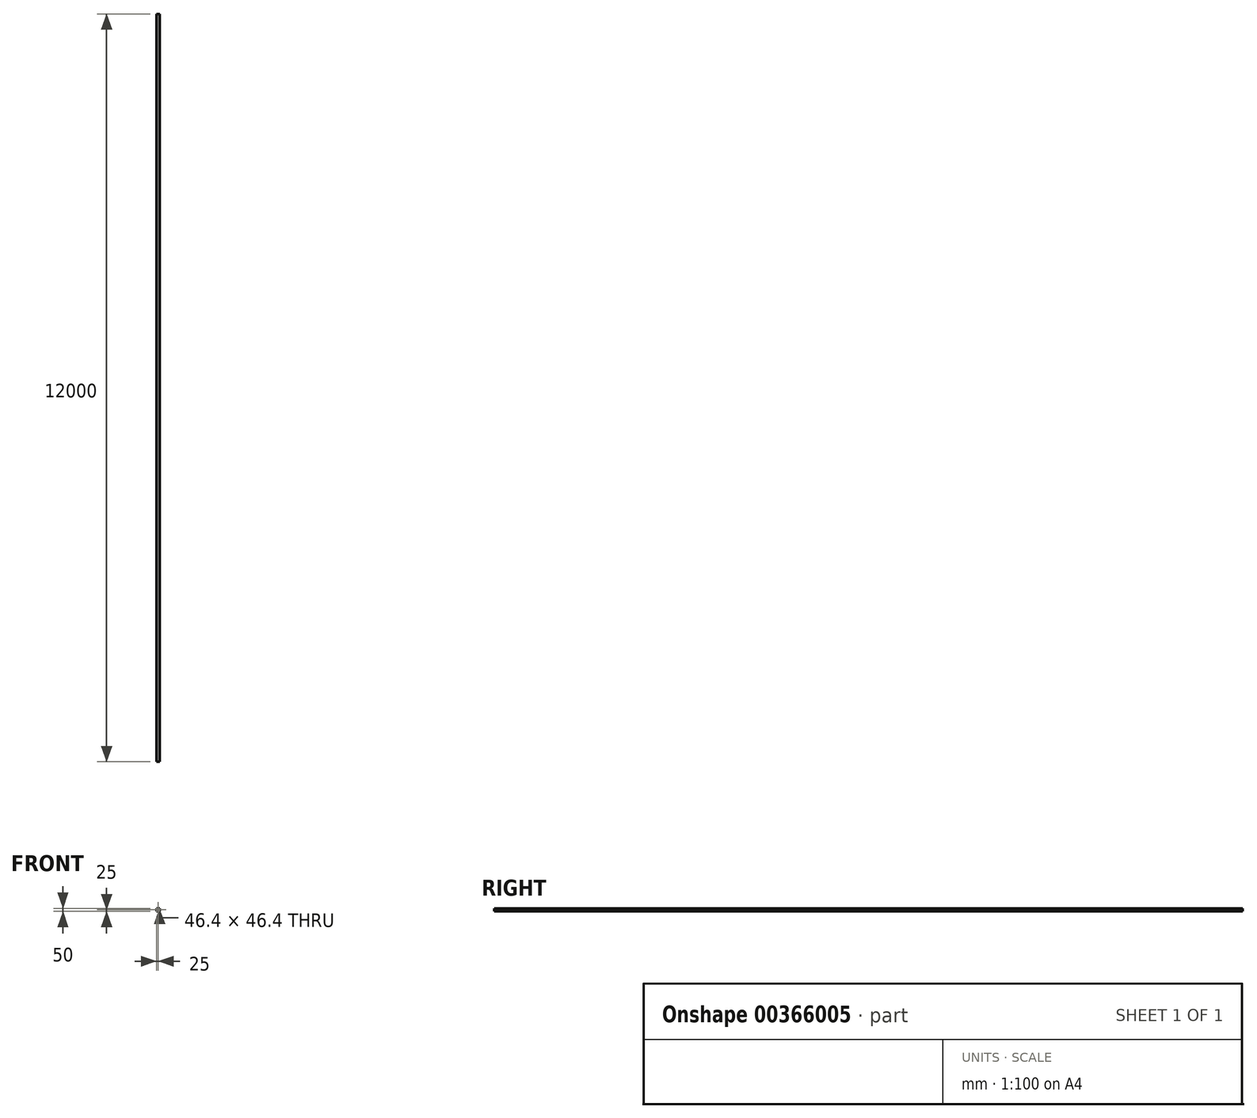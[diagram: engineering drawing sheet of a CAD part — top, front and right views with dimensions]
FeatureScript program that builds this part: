
annotation { "Feature Type Name" : "Feature", "Feature Type Description" : "" }
export const myFeature = defineFeature(function(context is Context, id is Id, definition is map)
    precondition{}
    {
        {
            var Q0;
            Q0=qCreatedBy(makeId("Front.planeOp"),FACE);
            var sketch = newSketch(context, id + "F0", { "sketchPlane" : qUnion([Q0])});
            skLineSegment(sketch, "E0.bottom", {"start": v(0, 0) * mm, "end": v(50, 0) * mm});
            skLineSegment(sketch, "E0.top", {"start": v(0, 50) * mm, "end": v(50, 50) * mm});
            skLineSegment(sketch, "E0.left", {"start": v(0, 0) * mm, "end": v(0, 50) * mm});
            skLineSegment(sketch, "E0.right", {"start": v(50, 0) * mm, "end": v(50, 50) * mm});
            skLineSegment(sketch, "E1.0", {"start": v(1.8, 48.2) * mm, "end": v(48.2, 48.2) * mm});
            skLineSegment(sketch, "E1.1", {"start": v(1.8, 1.8) * mm, "end": v(1.8, 48.2) * mm});
            skLineSegment(sketch, "E1.2", {"start": v(1.8, 1.8) * mm, "end": v(48.2, 1.8) * mm});
            skLineSegment(sketch, "E1.3", {"start": v(48.2, 1.8) * mm, "end": v(48.2, 48.2) * mm});
            skSolve(sketch);
        }
        {
            var Q0;
            Q0=makeQuery(id+"F0.imprint","IMPRINT",FACE,{"disambiguationData":[TD([[makeQuery(id+"F0.imprint","IMPRINT",EDGE,{"derivedFrom":sQuery(id+"F0.wireOp",EDGE,"E0.bottom")}),1.0]])]});
            extrude(context, id + "F1", {"entities" : qUnion([Q0]), "depth" : 12000 * mm});
        }
    });
